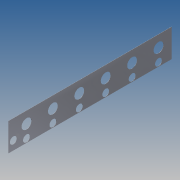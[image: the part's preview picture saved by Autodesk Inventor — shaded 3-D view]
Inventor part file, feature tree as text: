
AUTODESK INVENTOR PART (.ipt)
format: ipt  version: 2014 SP1 (Build 180222100, 222)  size: 592,896 bytes
history: native  units: in
note: dims shown in document units (in); Inventor stores cm internally (conversion verified against a paired STEP export)
features: other x5, sketch x5
ambient origin geometry x8: Origin, YZ Plane, XZ Plane, XY Plane, X Axis, Y Axis, Z Axis, Center Point
bodies: Solid1 (feature_tree)
feature tree (10):
  other  "ringOuter_Full.ipt"
  other  "Solid1::ringOuter_Full.ipt"
  other  "TaggingFeature1"
  sketch  "Sketch1"  dims[d0=0.3937in]
  sketch  "Sketch2"  dims[d1=73.1722in d2=10.0in d3=0.0in d5=0.06in d6=3.5433in d7=5.9in d8=5.9624in d9=2.3622in d11=9.4248in d16=3.5433in d23=2.4803in d24=1.3976in d25=2.3622in d27=9.4248in d32=5.9624in d33=2.4803in d40=2.4803in d41=2.4803in d109=2.75in d110=4.7124in d212=0.5in d213=1.0in d214=1.1811in d216=4.0in d221=0.0394in]
  sketch  "Sketch3"  dims[d177=1.7408in]
  sketch  "Sketch4"
  sketch  "Sketch19"
  other  "Srf1"
  other  "Srf1::Derived"
